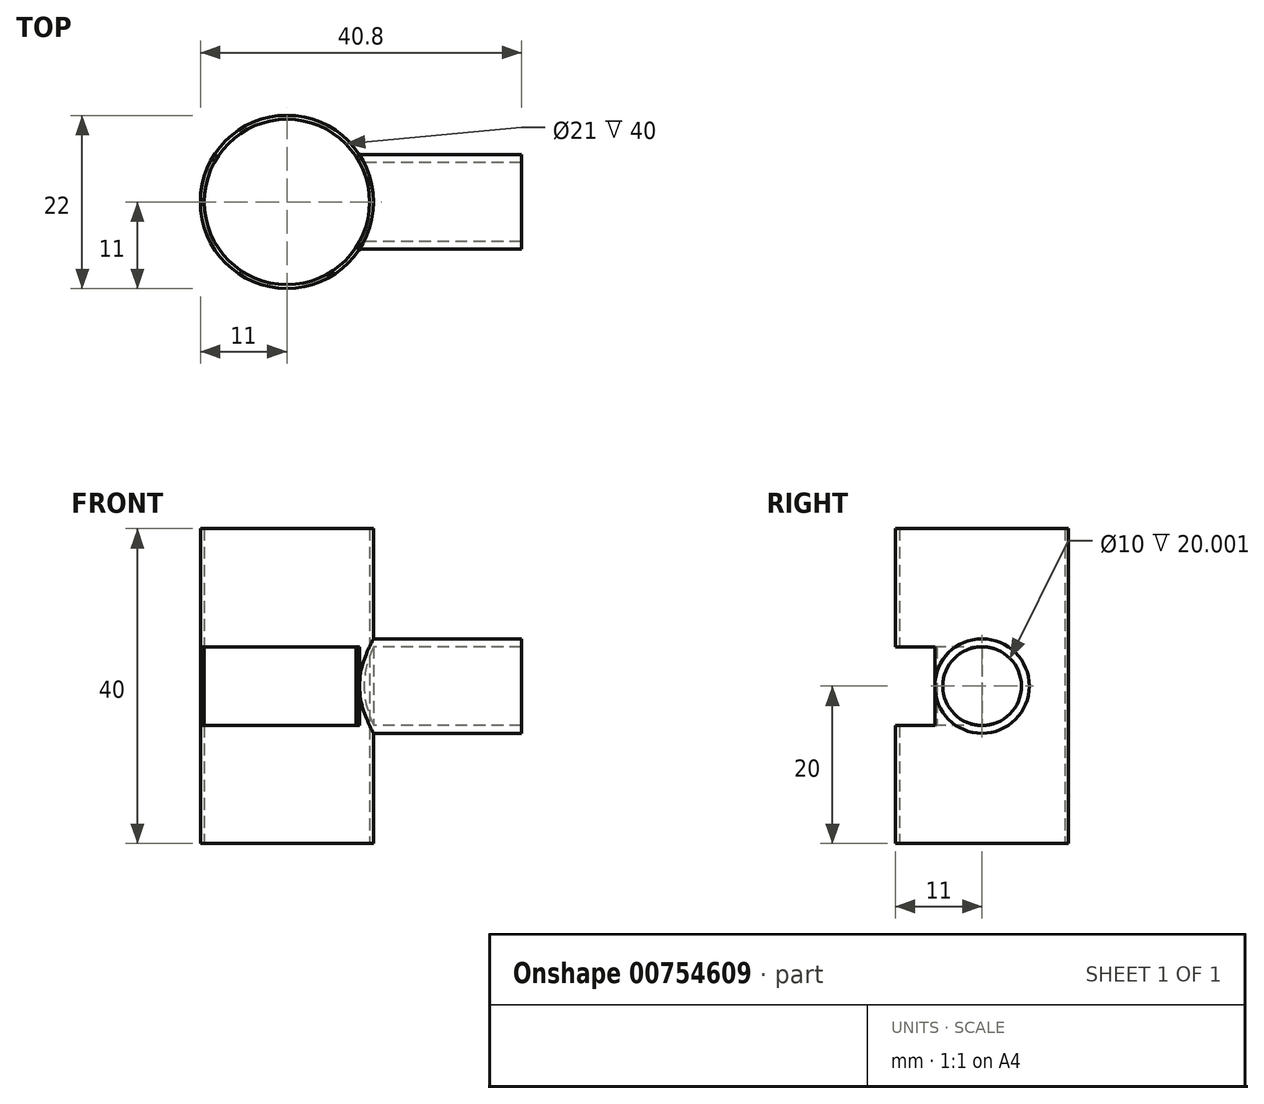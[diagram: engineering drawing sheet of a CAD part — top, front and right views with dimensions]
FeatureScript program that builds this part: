
annotation { "Feature Type Name" : "Feature", "Feature Type Description" : "" }
export const myFeature = defineFeature(function(context is Context, id is Id, definition is map)
    precondition{}
    {
        {
            var Q0;
            Q0=qCreatedBy(makeId("Top.planeOp"),FACE);
            var sketch = newSketch(context, id + "F0", { "sketchPlane" : qUnion([Q0])});
            skCircle(sketch, "E0", {"center": v(0, 0) * mm, "radius": 11 * mm});
            skCircle(sketch, "E1", {"center": v(0, 0) * mm, "radius": 10.5 * mm});
            skLineSegment(sketch, "E2", {"start": v(-10.5, 0) * mm, "end": v(-11, 0) * mm});
            skLineSegment(sketch, "E3", {"start": v(10.5, 0) * mm, "end": v(11, 0) * mm});
            skLineSegment(sketch, "E4", {"start": v(-11, 0) * mm, "end": v(-11, -15) * mm});
            skLineSegment(sketch, "E5", {"start": v(-11, -15) * mm, "end": v(11, -15) * mm});
            skLineSegment(sketch, "E6", {"start": v(11, -15) * mm, "end": v(11, 0) * mm});
            skLineSegment(sketch, "E7", {"start": v(9.8, -5) * mm, "end": v(29.8, -5) * mm});
            skLineSegment(sketch, "E8", {"start": v(9.8, 5) * mm, "end": v(29.8, 5) * mm});
            skLineSegment(sketch, "E9", {"start": v(29.8, 5) * mm, "end": v(29.8, -5) * mm});
            skLineSegment(sketch, "E10", {"start": v(29.8, 5) * mm, "end": v(29.8, 6) * mm});
            skLineSegment(sketch, "E11", {"start": v(29.8, -5) * mm, "end": v(29.8, -6) * mm});
            skLineSegment(sketch, "E12", {"start": v(29.8, -6) * mm, "end": v(9.22, -6) * mm});
            skLineSegment(sketch, "E13", {"start": v(29.8, 6) * mm, "end": v(9.22, 6) * mm});
            skLineSegment(sketch, "E14", {"start": v(-10.5, 0) * mm, "end": v(10.5, 0) * mm});
            skLineSegment(sketch, "E15", {"start": v(9.22, -6) * mm, "end": v(0, 0) * mm});
            skSolve(sketch);
        }
        {
            var Q0;
            {var subQ0=sQuery(id+"F0.wireOp",EDGE,"E2");Q0=makeQuery(id+"F0.imprint","IMPRINT",FACE,{"disambiguationData":[TD([[makeQuery(id+"F0.imprint","IMPRINT",EDGE,{"derivedFrom":subQ0}),-1.0]])]});}
            var Q1;
            {var subQ0=sQuery(id+"F0.wireOp",EDGE,"E2");Q1=makeQuery(id+"F0.imprint","IMPRINT",FACE,{"disambiguationData":[TD([[makeQuery(id+"F0.imprint","IMPRINT",EDGE,{"derivedFrom":subQ0}),1.0]])]});}
            var Q2;
            {var subQ0=sQuery(id+"F0.wireOp",EDGE,"E3");Q2=makeQuery(id+"F0.imprint","IMPRINT",FACE,{"disambiguationData":[TD([[makeQuery(id+"F0.imprint","IMPRINT",EDGE,{"derivedFrom":subQ0}),-1.0]])]});}
            extrude(context, id + "F1", {"entities" : qUnion([Q0, Q1, Q2]), "endBound" : BoundingType.SYMMETRIC, "depth" : 40 * mm, "offsetDistance" : 25 * mm});
        }
        {
            var Q0;
            {var subQ0=sQuery(id+"F0.wireOp",EDGE,"E14");var subQ3=sQuery(id+"F0.wireOp",EDGE,"E15");var subQ5=makeQuery(id+"F0.imprint","INTERSECT",VERTEX,{"derivedFrom":[subQ0,subQ3]});Q0=makeQuery(id+"F0.imprint","IMPRINT",FACE,{"disambiguationData":[TD([[makeQuery(id+"F0.imprint","IMPRINT",EDGE,{"disambiguationData":[TD([[subQ5,1.0]])],"derivedFrom":subQ3}),1.0]])]});}
            var Q1;
            {var subQ6=sQuery(id+"F0.wireOp",EDGE,"E4");Q1=makeQuery(id+"F0.imprint","IMPRINT",FACE,{"disambiguationData":[TD([[makeQuery(id+"F0.imprint","IMPRINT",EDGE,{"derivedFrom":subQ6}),1.0]])]});}
            var Q2;
            {var subQ0=sQuery(id+"F0.wireOp",EDGE,"E2");Q2=makeQuery(id+"F0.imprint","IMPRINT",FACE,{"disambiguationData":[TD([[makeQuery(id+"F0.imprint","IMPRINT",EDGE,{"derivedFrom":subQ0}),1.0]])]});}
            extrude(context, id + "F2", {"entities" : qUnion([Q0, Q1, Q2]), "operationType" : NewBodyOperationType.REMOVE, "endBound" : BoundingType.SYMMETRIC, "depth" : 10 * mm, "offsetDistance" : 25 * mm});
        }
        {
            var Q0;
            {var subQ0=sQuery(id+"F0.wireOp",EDGE,"E8");Q0=makeQuery(id+"F0.imprint","IMPRINT",FACE,{"disambiguationData":[TD([[makeQuery(id+"F0.imprint","IMPRINT",EDGE,{"derivedFrom":subQ0}),1.0]])]});}
            var Q1;
            Q1=sQuery(id+"F0.wireOp",EDGE,"E14");
            revolve(context, id + "F3", {"operationType" : NewBodyOperationType.ADD, "surfaceOperationType" : NewSurfaceOperationType.NEW, "entities" : qUnion([Q0]), "axis" : qUnion([Q1]), "revolveType" : RevolveType.FULL});
        }
        {
            var Q0;
            {var subQ0=sQuery(id+"F0.wireOp",EDGE,"E14");var subQ4=makeQuery(id+"F0.imprint","INTERSECT",VERTEX,{"derivedFrom":[subQ0,sQuery(id+"F0.wireOp",EDGE,"E15")]});Q0=makeQuery(id+"F0.imprint","IMPRINT",FACE,{"disambiguationData":[TD([[makeQuery(id+"F0.imprint","IMPRINT",EDGE,{"disambiguationData":[TD([[subQ4,1.0]])],"derivedFrom":subQ0}),1.0]])]});}
            var Q1;
            {var subQ0=sQuery(id+"F0.wireOp",EDGE,"E14");var subQ3=sQuery(id+"F0.wireOp",EDGE,"E15");var subQ5=makeQuery(id+"F0.imprint","INTERSECT",VERTEX,{"derivedFrom":[subQ0,subQ3]});Q1=makeQuery(id+"F0.imprint","IMPRINT",FACE,{"disambiguationData":[TD([[makeQuery(id+"F0.imprint","IMPRINT",EDGE,{"disambiguationData":[TD([[subQ5,1.0]])],"derivedFrom":subQ3}),1.0]])]});}
            var Q2;
            {var subQ0=sQuery(id+"F0.wireOp",EDGE,"E14");var subQ3=sQuery(id+"F0.wireOp",EDGE,"E15");var subQ5=makeQuery(id+"F0.imprint","INTERSECT",VERTEX,{"derivedFrom":[subQ0,subQ3]});Q2=makeQuery(id+"F0.imprint","IMPRINT",FACE,{"disambiguationData":[TD([[makeQuery(id+"F0.imprint","IMPRINT",EDGE,{"disambiguationData":[TD([[subQ5,1.0]])],"derivedFrom":subQ3}),-1.0]])]});}
            extrude(context, id + "F4", {"entities" : qUnion([Q0, Q1, Q2]), "operationType" : NewBodyOperationType.REMOVE, "endBound" : BoundingType.SYMMETRIC, "depth" : 25 * mm, "offsetDistance" : 25 * mm});
        }
    });
